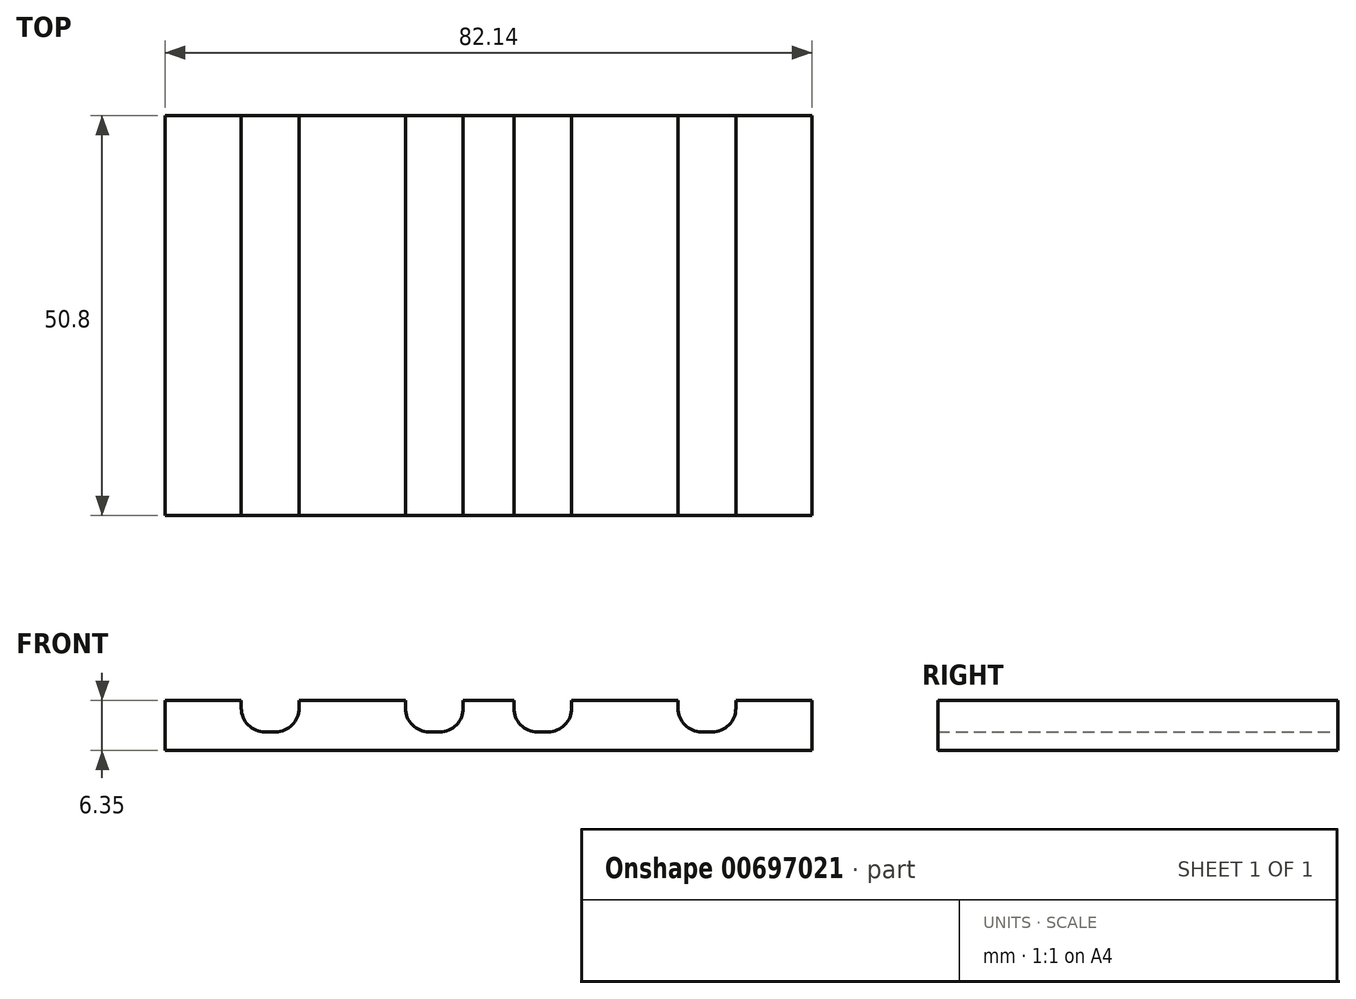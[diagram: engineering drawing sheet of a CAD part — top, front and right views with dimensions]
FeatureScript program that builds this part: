
annotation { "Feature Type Name" : "Feature", "Feature Type Description" : "" }
export const myFeature = defineFeature(function(context is Context, id is Id, definition is map)
    precondition{}
    {
        {
            var Q0;
            Q0=qCreatedBy(makeId("Front.planeOp"),FACE);
            var sketch = newSketch(context, id + "F0", { "sketchPlane" : qUnion([Q0])});
            skLineSegment(sketch, "E0.bottom", {"start": v(-41.07, 74.03) * mm, "end": v(-10.56, 74.03) * mm});
            skLineSegment(sketch, "E0.top", {"start": v(-41.07, 67.68) * mm, "end": v(41.07, 67.68) * mm});
            skLineSegment(sketch, "E0.left", {"start": v(-41.07, 74.03) * mm, "end": v(-41.07, 67.68) * mm});
            skLineSegment(sketch, "E0.right", {"start": v(41.07, 74.03) * mm, "end": v(41.07, 67.68) * mm});
            skLineSegment(sketch, "E1.bottom", {"start": v(-10.56, 73.03) * mm, "end": v(-3.21, 73.03) * mm});
            skLineSegment(sketch, "E1.top", {"start": v(-10.56, 79.6) * mm, "end": v(-3.21, 79.6) * mm});
            skLineSegment(sketch, "E1.left", {"start": v(-10.56, 73.03) * mm, "end": v(-10.56, 74.03) * mm});
            skLineSegment(sketch, "E1.right", {"start": v(-3.21, 73.03) * mm, "end": v(-3.21, 74.03) * mm});
            skLineSegment(sketch, "E2.bottom", {"start": v(-7.56, 70.03) * mm, "end": v(-7.56, 70.03) * mm});
            skLineSegment(sketch, "E2.top", {"start": v(-7.56, 73.03) * mm, "end": v(-6.21, 73.03) * mm});
            skLineSegment(sketch, "E2.left", {"start": v(-7.56, 70.03) * mm, "end": v(-7.56, 73.03) * mm});
            skLineSegment(sketch, "E2.right", {"start": v(-6.21, 70.03) * mm, "end": v(-6.21, 73.03) * mm});
            skLineSegment(sketch, "E3", {"start": v(-3.21, 74.03) * mm, "end": v(-3.21, 79.6) * mm});
            skLineSegment(sketch, "E4", {"start": v(-10.56, 74.03) * mm, "end": v(-10.56, 79.6) * mm});
            skLineSegment(sketch, "E5", {"start": v(-7.56, 70.03) * mm, "end": v(-6.21, 70.03) * mm});
            skLineSegment(sketch, "E6", {"start": v(-3.21, 74.03) * mm, "end": v(-3.21, 74.03) * mm});
            skLineSegment(sketch, "E7", {"start": v(-10.56, 74.03) * mm, "end": v(-10.38, 74.03) * mm});
            skArc(sketch, "E8", {"start": v(-7.56, 70.03) * mm, "mid": v(-5.1, 74.77) * mm, "end": v(-10.38, 74.03) * mm});
            skArc(sketch, "E9", {"start": v(-10.56, 73.03) * mm, "mid": v(-9.68, 70.91) * mm, "end": v(-7.56, 70.03) * mm});
            skArc(sketch, "E10", {"start": v(-6.27, 70.03) * mm, "mid": v(-4.11, 70.9) * mm, "end": v(-3.21, 73.03) * mm});
            skArc(sketch, "E11", {"start": v(-3.21, 73.03) * mm, "mid": v(-3.25, 73.54) * mm, "end": v(-3.38, 74.03) * mm});
            skLineSegment(sketch, "E12", {"start": v(-3.21, 74.03) * mm, "end": v(41.07, 74.03) * mm});
            skArc(sketch, "E13", {"start": v(-10.4, 74) * mm, "mid": v(-10.52, 73.53) * mm, "end": v(-10.56, 73.03) * mm});
            skArc(sketch, "E14", {"start": v(-3.38, 74.03) * mm, "mid": v(-8.64, 74.8) * mm, "end": v(-6.27, 70.03) * mm});
            skLineSegment(sketch, "E15", {"start": v(-10.38, 74.03) * mm, "end": v(-3.38, 74.03) * mm});
            skLineSegment(sketch, "E16", {"start": v(-3.38, 74.03) * mm, "end": v(-3.21, 74.03) * mm});
            skArc(sketch, "E17", {"start": v(-10.38, 74.03) * mm, "mid": v(-10.39, 74.02) * mm, "end": v(-10.4, 74) * mm});
            skLineSegment(sketch, "E18.bottom", {"start": v(-31.4, 73.03) * mm, "end": v(-24.06, 73.03) * mm});
            skLineSegment(sketch, "E18.top", {"start": v(-31.4, 79.6) * mm, "end": v(-24.06, 79.6) * mm});
            skLineSegment(sketch, "E18.left", {"start": v(-31.4, 73.03) * mm, "end": v(-31.4, 74.03) * mm});
            skLineSegment(sketch, "E18.right", {"start": v(-24.06, 73.03) * mm, "end": v(-24.06, 73.92) * mm});
            skLineSegment(sketch, "E19.top", {"start": v(-27.06, 73.03) * mm, "end": v(-26.4, 73.03) * mm});
            skLineSegment(sketch, "E19.right", {"start": v(-27.06, 70.03) * mm, "end": v(-27.06, 73.03) * mm});
            skLineSegment(sketch, "E20", {"start": v(-24.06, 73.92) * mm, "end": v(-24.06, 79.6) * mm});
            skLineSegment(sketch, "E21", {"start": v(-31.4, 74.03) * mm, "end": v(-31.4, 79.6) * mm});
            skLineSegment(sketch, "E22", {"start": v(-28.4, 70.03) * mm, "end": v(-27.06, 70.03) * mm});
            skLineSegment(sketch, "E23", {"start": v(-24.06, 74.03) * mm, "end": v(-24.06, 74.03) * mm});
            skLineSegment(sketch, "E24", {"start": v(-31.4, 74.03) * mm, "end": v(-31.24, 74.03) * mm});
            skArc(sketch, "E25", {"start": v(-28.4, 70.03) * mm, "mid": v(-25.96, 74.77) * mm, "end": v(-31.24, 74.03) * mm});
            skArc(sketch, "E26", {"start": v(-31.4, 73.03) * mm, "mid": v(-30.53, 70.91) * mm, "end": v(-28.4, 70.03) * mm});
            skArc(sketch, "E27", {"start": v(-27.12, 70.03) * mm, "mid": v(-24.96, 70.9) * mm, "end": v(-24.06, 73.03) * mm});
            skArc(sketch, "E28", {"start": v(-24.06, 73.03) * mm, "mid": v(-24.1, 73.54) * mm, "end": v(-24.24, 74.03) * mm});
            skArc(sketch, "E29", {"start": v(-31.25, 74) * mm, "mid": v(-31.37, 73.53) * mm, "end": v(-31.4, 73.03) * mm});
            skArc(sketch, "E30", {"start": v(-24.24, 74.03) * mm, "mid": v(-29.5, 74.8) * mm, "end": v(-27.12, 70.03) * mm});
            skLineSegment(sketch, "E31", {"start": v(-31.24, 74.03) * mm, "end": v(-24.24, 74.03) * mm});
            skLineSegment(sketch, "E32", {"start": v(-24.24, 74.03) * mm, "end": v(-24.06, 74.03) * mm});
            skArc(sketch, "E33", {"start": v(-31.24, 74.03) * mm, "mid": v(-31.24, 74.02) * mm, "end": v(-31.25, 74) * mm});
            skLineSegment(sketch, "E34.bottom", {"start": v(3.21, 73.03) * mm, "end": v(10.56, 73.03) * mm});
            skLineSegment(sketch, "E34.top", {"start": v(3.21, 79.6) * mm, "end": v(10.56, 79.6) * mm});
            skLineSegment(sketch, "E34.left", {"start": v(3.21, 73.03) * mm, "end": v(3.21, 74.03) * mm});
            skLineSegment(sketch, "E34.right", {"start": v(10.56, 73.03) * mm, "end": v(10.56, 73.92) * mm});
            skLineSegment(sketch, "E35.right", {"start": v(7.56, 70.03) * mm, "end": v(7.56, 73.03) * mm});
            skLineSegment(sketch, "E36", {"start": v(10.56, 73.92) * mm, "end": v(10.56, 79.6) * mm});
            skLineSegment(sketch, "E37", {"start": v(3.21, 74.03) * mm, "end": v(3.21, 79.6) * mm});
            skLineSegment(sketch, "E38", {"start": v(6.21, 70.03) * mm, "end": v(7.56, 70.03) * mm});
            skLineSegment(sketch, "E39", {"start": v(10.56, 74.03) * mm, "end": v(10.56, 74.03) * mm});
            skLineSegment(sketch, "E40", {"start": v(3.21, 74.03) * mm, "end": v(3.38, 74.03) * mm});
            skArc(sketch, "E41", {"start": v(6.21, 70.03) * mm, "mid": v(8.66, 74.77) * mm, "end": v(3.38, 74.03) * mm});
            skArc(sketch, "E42", {"start": v(3.21, 73.03) * mm, "mid": v(4.09, 70.91) * mm, "end": v(6.21, 70.03) * mm});
            skArc(sketch, "E43", {"start": v(7.5, 70.03) * mm, "mid": v(9.66, 70.9) * mm, "end": v(10.56, 73.03) * mm});
            skArc(sketch, "E44", {"start": v(10.56, 73.03) * mm, "mid": v(10.51, 73.54) * mm, "end": v(10.38, 74.03) * mm});
            skArc(sketch, "E45", {"start": v(3.37, 74) * mm, "mid": v(3.25, 73.53) * mm, "end": v(3.21, 73.03) * mm});
            skArc(sketch, "E46", {"start": v(10.38, 74.03) * mm, "mid": v(5.12, 74.8) * mm, "end": v(7.5, 70.03) * mm});
            skLineSegment(sketch, "E47", {"start": v(3.38, 74.03) * mm, "end": v(10.38, 74.03) * mm});
            skLineSegment(sketch, "E48", {"start": v(10.38, 74.03) * mm, "end": v(10.56, 74.03) * mm});
            skArc(sketch, "E49", {"start": v(3.38, 74.03) * mm, "mid": v(3.38, 74.02) * mm, "end": v(3.37, 74) * mm});
            skLineSegment(sketch, "E50.bottom", {"start": v(24.06, 73.03) * mm, "end": v(31.4, 73.03) * mm});
            skLineSegment(sketch, "E50.top", {"start": v(24.06, 79.6) * mm, "end": v(31.4, 79.6) * mm});
            skLineSegment(sketch, "E50.left", {"start": v(24.06, 73.03) * mm, "end": v(24.06, 74.03) * mm});
            skLineSegment(sketch, "E50.right", {"start": v(31.4, 73.03) * mm, "end": v(31.4, 74.03) * mm});
            skLineSegment(sketch, "E51.right", {"start": v(28.4, 70.03) * mm, "end": v(28.4, 73.03) * mm});
            skLineSegment(sketch, "E52", {"start": v(31.4, 74.03) * mm, "end": v(31.4, 79.6) * mm});
            skLineSegment(sketch, "E53", {"start": v(24.06, 74.03) * mm, "end": v(24.06, 79.6) * mm});
            skLineSegment(sketch, "E54", {"start": v(27.06, 70.03) * mm, "end": v(28.4, 70.03) * mm});
            skLineSegment(sketch, "E55", {"start": v(31.4, 74.03) * mm, "end": v(31.4, 74.03) * mm});
            skLineSegment(sketch, "E56", {"start": v(24.06, 74.03) * mm, "end": v(24.24, 74.03) * mm});
            skArc(sketch, "E57", {"start": v(27.06, 70.03) * mm, "mid": v(29.51, 74.77) * mm, "end": v(24.24, 74.03) * mm});
            skArc(sketch, "E58", {"start": v(24.06, 73.03) * mm, "mid": v(24.94, 70.91) * mm, "end": v(27.06, 70.03) * mm});
            skArc(sketch, "E59", {"start": v(28.35, 70.03) * mm, "mid": v(30.5, 70.9) * mm, "end": v(31.4, 73.03) * mm});
            skArc(sketch, "E60", {"start": v(31.4, 73.03) * mm, "mid": v(31.37, 73.54) * mm, "end": v(31.24, 74.03) * mm});
            skArc(sketch, "E61", {"start": v(24.23, 74) * mm, "mid": v(24.1, 73.53) * mm, "end": v(24.06, 73.03) * mm});
            skArc(sketch, "E62", {"start": v(31.24, 74.03) * mm, "mid": v(25.98, 74.8) * mm, "end": v(28.35, 70.03) * mm});
            skLineSegment(sketch, "E63", {"start": v(24.24, 74.03) * mm, "end": v(31.24, 74.03) * mm});
            skLineSegment(sketch, "E64", {"start": v(31.24, 74.03) * mm, "end": v(31.4, 74.03) * mm});
            skArc(sketch, "E65", {"start": v(24.24, 74.03) * mm, "mid": v(24.23, 74.02) * mm, "end": v(24.23, 74) * mm});
            skLineSegment(sketch, "E66", {"start": v(-28.4, 73.03) * mm, "end": v(-28.4, 70.03) * mm});
            skLineSegment(sketch, "E67", {"start": v(6.21, 73.03) * mm, "end": v(6.21, 70.03) * mm});
            skPoint(sketch, "E68", {"position": v(-27.74, 75.96) * mm});
            skPoint(sketch, "E69", {"position": v(-6.88, 75.96) * mm});
            skPoint(sketch, "E70", {"position": v(6.88, 75.96) * mm});
            skPoint(sketch, "E71", {"position": v(27.74, 75.96) * mm});
            skSolve(sketch);
        }
        {
            var Q0;
            Q0=makeQuery(id+"F0.imprint","IMPRINT",FACE,{"disambiguationData":[TD([[makeQuery(id+"F0.imprint","IMPRINT",EDGE,{"derivedFrom":sQuery(id+"F0.wireOp",EDGE,"E0.top")}),1.0]])]});
            extrude(context, id + "F1", {"entities" : qUnion([Q0]), "depth" : 50.8 * mm, "offsetDistance" : 25.4 * mm});
        }
    });
